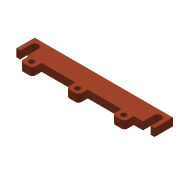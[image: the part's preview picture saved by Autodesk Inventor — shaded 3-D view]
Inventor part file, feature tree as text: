
AUTODESK INVENTOR PART (.ipt)
format: ipt  version: 2013 (Build 170138000, 138)  size: 175,616 bytes
history: native  units: in
note: dims shown in document units (in); Inventor stores cm internally (conversion verified against a paired STEP export)
features: fillet x6, extrude x3, sketch x3
ambient origin geometry x8: Origin, YZ Plane, XZ Plane, XY Plane, X Axis, Y Axis, Z Axis, Center Point
bodies: Solid1 (feature_tree)
feature tree (12):
  extrude  "Extrusion1"  Depth=0.4724in
  fillet  "Fillet1"  Radius=0.8465in
  fillet  "Fillet2"  Radius=1.1811in
  fillet  "Fillet3"  Radius=1.1811in
  fillet  "Fillet4"  Radius=0.2362in
  fillet  "Fillet5"  Radius=0.2362in
  fillet  "Fillet6"  Radius=0.2362in
  extrude  "Extrusion2"  Depth=0.315in
  extrude  "Extrusion4"  Depth=0.1969in TaperAngle=0.0deg
  sketch  "Sketch1"  dims[d0=3.5433in d3=0.4724in d4=0.8465in d5=1.1811in d6=1.1811in d7=0.2362in d8=0.2362in d9=0.2362in]
  sketch  "Sketch2"  dims[d10=0.315in d11=0.315in]
  sketch  "Sketch4"  dims[d12=0.315in d13=0.1969in d14=0.0in d15=0.0787in d16=0.0787in d17=0.0787in d18=0.0787in d19=0.0787in d20=0.0787in d23=0.1378in d29=0.1378in d30=0.1378in d31=0.3937in d32=0.0in d47=0.0984in d48=0.1575in d49=0.0984in d50=0.1575in d51=0.0984in d52=0.1575in d53=0.1969in d54=0.1969in d55=0.1969in d56=0.1969in d57=0.1969in d58=0.1969in d59=0.3937in d60=0.0in]
